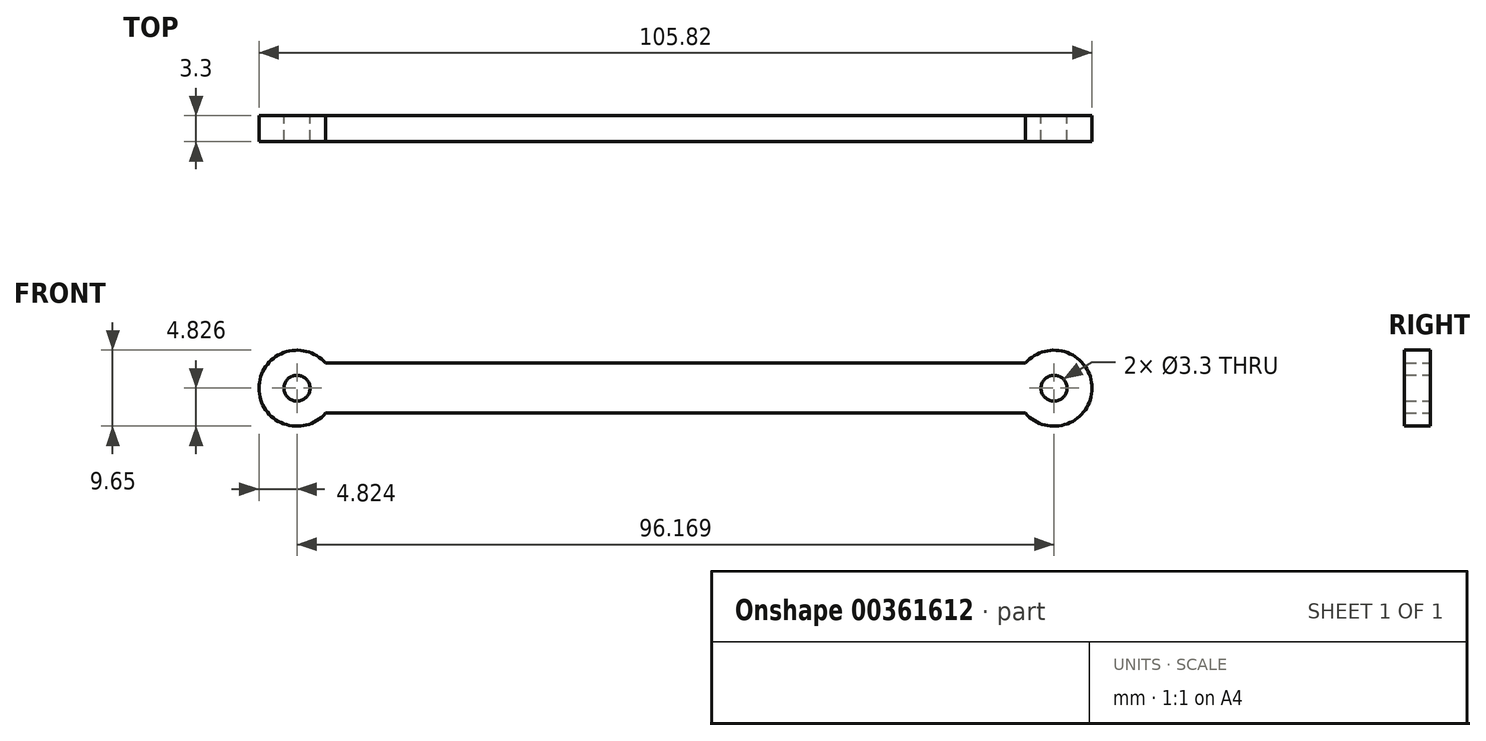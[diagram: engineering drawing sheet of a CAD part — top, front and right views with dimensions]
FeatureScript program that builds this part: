
annotation { "Feature Type Name" : "Feature", "Feature Type Description" : "" }
export const myFeature = defineFeature(function(context is Context, id is Id, definition is map)
    precondition{}
    {
        {
            var Q0;
            Q0=qCreatedBy(makeId("Front.planeOp"),FACE);
            var sketch = newSketch(context, id + "F0", { "sketchPlane" : qUnion([Q0])});
            skLineSegment(sketch, "E0", {"start": v(0, 8.84) * mm, "end": v(47.58, 8.84) * mm});
            skLineSegment(sketch, "E1", {"start": v(0, 8.84) * mm, "end": v(-41.32, 8.84) * mm});
            skLineSegment(sketch, "E2", {"start": v(-41.32, 2.5) * mm, "end": v(47.58, 2.5) * mm});
            skArc(sketch, "E3", {"start": v(47.58, 2.5) * mm, "mid": v(56.04, 5.67) * mm, "end": v(47.58, 8.84) * mm});
            skArc(sketch, "E4", {"start": v(-41.32, 8.84) * mm, "mid": v(-49.78, 5.67) * mm, "end": v(-41.32, 2.5) * mm});
            skCircle(sketch, "E5", {"center": v(-44.96, 5.67) * mm, "radius": 1.65 * mm});
            skCircle(sketch, "E6", {"center": v(51.21, 5.67) * mm, "radius": 1.65 * mm});
            skSolve(sketch);
        }
        {
            var Q0;
            Q0 = qSketchRegion(id + "F0", true);
            extrude(context, id + "F1", {"entities" : qUnion([Q0]), "depth" : 3.3 * mm});
        }
    });
